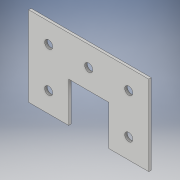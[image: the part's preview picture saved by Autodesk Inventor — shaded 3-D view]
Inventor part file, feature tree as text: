
AUTODESK INVENTOR PART (.ipt)
format: ipt  version: 2018 (Build 220112000, 112)  size: 113,664 bytes
history: native  units: in
note: dims shown in document units (in); Inventor stores cm internally (conversion verified against a paired STEP export)
features: extrude x1, sketch x1
ambient origin geometry x8: Origin, YZ Plane, XZ Plane, XY Plane, X Axis, Y Axis, Z Axis, Center Point
bodies: Body1 (feature_tree)
feature tree (2):
  extrude  "Extrusion2"  Depth=2.0in
  sketch  "Sketch1"  dims[d0=1.0in d1=2.0in d5=0.5in d6=1.0in d7=1.0in d11=0.2031in d14=1.0in d15=1.0in d16=1.0in d17=1.0in d18=0.0625in d19=0.0in]
